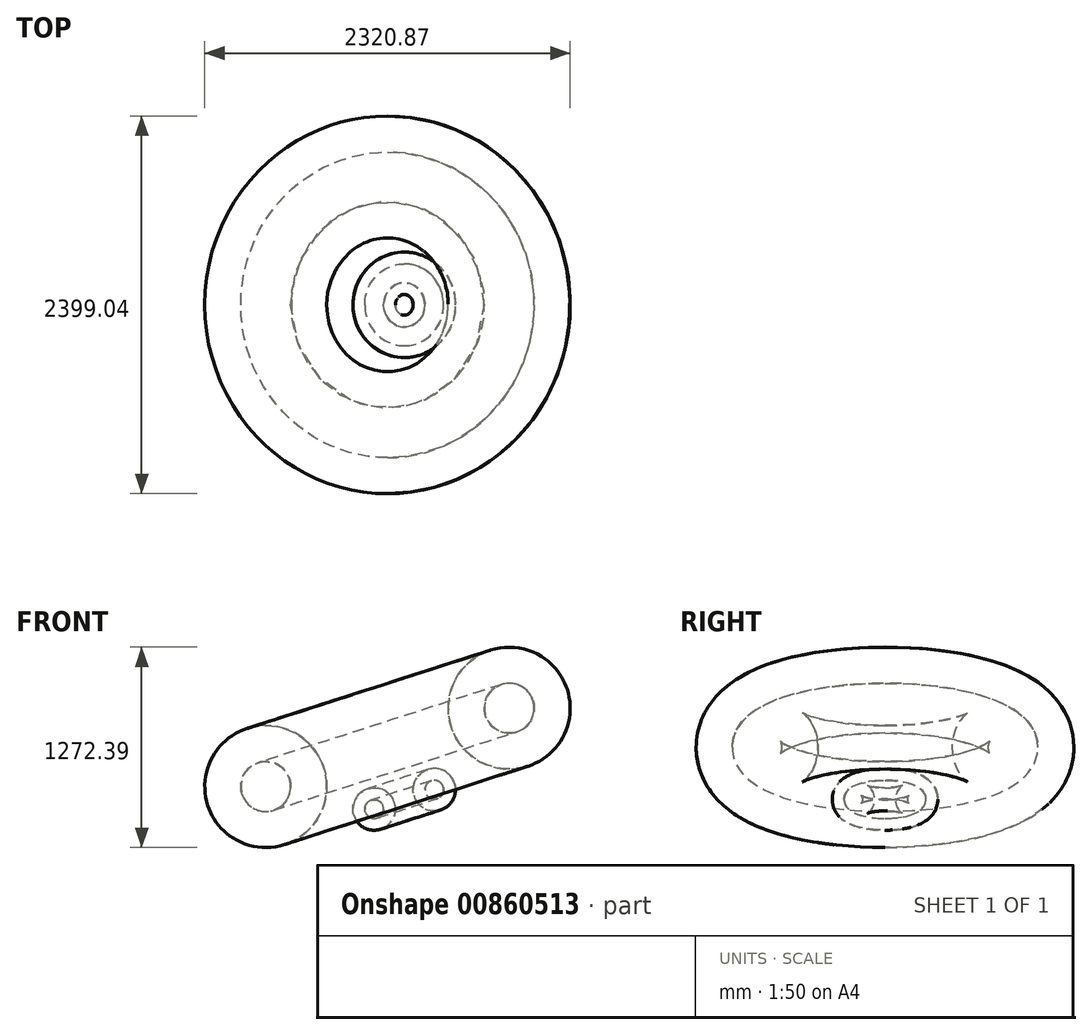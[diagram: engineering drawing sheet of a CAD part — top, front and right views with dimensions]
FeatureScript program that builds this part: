
annotation { "Feature Type Name" : "Feature", "Feature Type Description" : "" }
export const myFeature = defineFeature(function(context is Context, id is Id, definition is map)
    precondition{}
    {
        {
            var Q0;
            Q0=qCreatedBy(makeId("Front.planeOp"),FACE);
            var sketch = newSketch(context, id + "F0", { "sketchPlane" : qUnion([Q0])});
            skLineSegment(sketch, "E0", {"start": v(-397.66, 370.6) * mm, "end": v(-122.84, -483.03) * mm, "construction": true});
            skCircle(sketch, "E1", {"center": v(564.22, 33.31) * mm, "radius": 387.28 * mm});
            skCircle(sketch, "E2", {"center": v(564.22, 33.31) * mm, "radius": 158.23 * mm});
            skCircle(sketch, "E3", {"center": v(88.25, -484.6) * mm, "radius": 134.74 * mm});
            skCircle(sketch, "E4", {"center": v(88.25, -484.6) * mm, "radius": 59.3 * mm});
            skSolve(sketch);
        }
        {
            var Q0;
            Q0 = qSketchRegion(id + "F0", true);
            var Q1;
            Q1=sQuery(id+"F0.wireOp",EDGE,"E0");
            revolve(context, id + "F1", {"surfaceOperationType" : NewSurfaceOperationType.NEW, "entities" : qUnion([Q0]), "axis" : qUnion([Q1]), "revolveType" : RevolveType.FULL});
        }
        {
            var Q0;
            Q0 = qSketchRegion(id + "F0", true);
            var Q1;
            Q1=makeQuery(id+"F1.opRevolve","SWEPT_FACE",FACE,{"disambiguationData":[OSD([sQuery(id+"F0.wireOp",EDGE,"E1")])]});
            revolve(context, id + "F2", {"surfaceOperationType" : NewSurfaceOperationType.NEW, "entities" : qUnion([Q0]), "axis" : qUnion([Q1]), "revolveType" : RevolveType.FULL});
        }
    });
